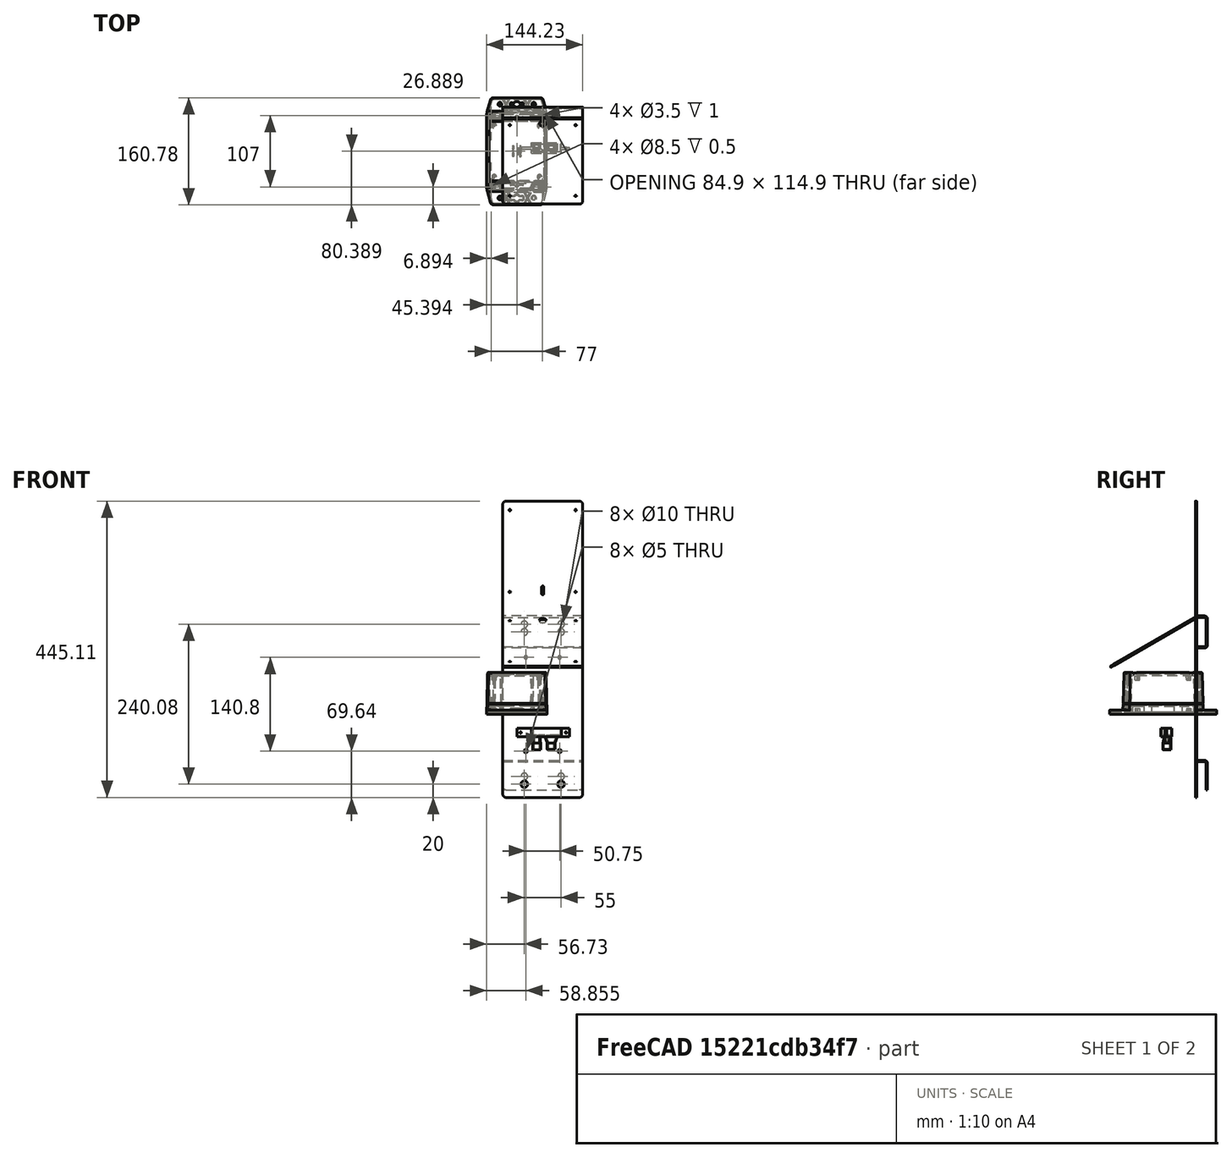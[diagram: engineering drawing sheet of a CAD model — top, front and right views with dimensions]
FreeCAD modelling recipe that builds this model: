
FCSTD DOCUMENT  (FreeCAD 0.19R24291 (Git))
Label: pzld_pm_vertical_wallmount
License: All rights reserved
LicenseURL: http://en.wikipedia.org/wiki/All_rights_reserved
objects: TechDraw::DrawViewDimension×19, Part::Feature×12, PartDesign::FeaturePython×10, Sketcher::SketchObject×7, TechDraw::DrawViewBalloon×4, TechDraw::DrawProjGroupItem×2, TechDraw::DrawProjGroup×2, PartDesign::Pad×1, App::Part×1, TechDraw::DrawSVGTemplate×1, TechDraw::DrawViewAnnotation×1, PartDesign::Fillet×1, PartDesign::Body×1, TechDraw::DrawPage×1
note: 34 computed .brp shape members not serialized (recipe doc carries the construction recipe); baked Part::Feature solids carry a one-line shape summary decoded from their .brp

FEATURE [Sketcher::SketchObject] Sketch
  FullyConstrained = true
  MapMode = 5
  Placement = pos=(0,0,0) rot=(1,0,0;1.5708rad)
  Support = -> [XZ_Plane]
  sketch-geometry (4):
    g0: LineSegment StartX=-60 StartY=-82.5 StartZ=0 EndX=60 EndY=-82.5 EndZ=0
    g1: LineSegment StartX=60 StartY=-82.5 StartZ=0 EndX=60 EndY=82.5 EndZ=0
    g2: LineSegment StartX=60 StartY=82.5 StartZ=0 EndX=-60 EndY=82.5 EndZ=0
    g3: LineSegment StartX=-60 StartY=82.5 StartZ=0 EndX=-60 EndY=-82.5 EndZ=0
  constraints (11):
    c: Coincident(g0,g1)
    c: Coincident(g1,g2)
    c: Coincident(g2,g3)
    c: Coincident(g3,g0)
    c: Horizontal(g0)
    c: Horizontal(g2)
    c: Vertical(g1)
    c: Vertical(g3)
    c: Symmetric(g1,g0,g-1)
    c: DistanceY(g3,g3) = 165
    c: DistanceX(g2,g2) = 120
FEATURE [PartDesign::Pad] Pad
  Direction = (1,1,1)
  Length = 2
  Length2 = 100
  Placement = pos=(0,0,0) rot=(1,0,0;1.5708rad)
  Profile = -> Sketch
  Type = 0
FEATURE [PartDesign::FeaturePython] Bend  label="Top to wall"  # WARN: FeaturePython — macro-defined, semantics opaque (R4)
  AutoMiter = true
  BaseFeature = -> Pad
  BendType = 0
  LengthList = [10]
  ReliefFactor = 0.7
  UseReliefFactor = false
  angle = 90
  baseObject = -> Pad [Edge10]
  bendAList = [90]
  extend1 = 0
  extend2 = 0
  gap1 = 0
  gap2 = 0
  invert = false
  kfactor = 0.5
  length = 10
  maxExtendDist = 5
  minGap = 0.1
  minReliefGap = 1
  miterangle1 = 0
  miterangle2 = 0
  offset = 0
  radius = 2
  reliefType = 0
  reliefd = 1
  reliefw = 0.8
  sketchflip = false
  sketchinvert = false
  unfold = false
FEATURE [PartDesign::FeaturePython] Bend001  label="Wall mount top"  # WARN: FeaturePython — macro-defined, semantics opaque (R4)
  AutoMiter = true
  BaseFeature = -> Bend
  BendType = 0
  LengthList = [40]
  ReliefFactor = 0.7
  UseReliefFactor = false
  angle = 90
  baseObject = -> Bend [Edge9]
  bendAList = [90]
  extend1 = 0
  extend2 = 0
  gap1 = 0
  gap2 = 0
  invert = true
  kfactor = 0.5
  length = 40
  maxExtendDist = 5
  minGap = 0.1
  minReliefGap = 1
  miterangle1 = 0
  miterangle2 = 0
  offset = 0
  radius = 2
  reliefType = 0
  reliefd = 1
  reliefw = 0.8
  sketchflip = false
  sketchinvert = false
  unfold = false
FEATURE [PartDesign::FeaturePython] Bend002  label="Top to solar"  # WARN: FeaturePython — macro-defined, semantics opaque (R4)
  AutoMiter = true
  BaseFeature = -> Bend001
  BendType = 0
  LengthList = [10]
  ReliefFactor = 0.7
  UseReliefFactor = false
  angle = 90
  baseObject = -> Bend001 [Edge9]
  bendAList = [90]
  extend1 = 0
  extend2 = 0
  gap1 = 0
  gap2 = 0
  invert = true
  kfactor = 0.5
  length = 10
  maxExtendDist = 5
  minGap = 0.1
  minReliefGap = 1
  miterangle1 = 0
  miterangle2 = 0
  offset = 0
  radius = 2
  reliefType = 0
  reliefd = 1
  reliefw = 0.8
  sketchflip = false
  sketchinvert = false
  unfold = false
FEATURE [PartDesign::FeaturePython] Bend003  label="Bottom to wall"  # WARN: FeaturePython — macro-defined, semantics opaque (R4)
  AutoMiter = true
  BaseFeature = -> Bend002
  BendType = 0
  LengthList = [10]
  ReliefFactor = 0.7
  UseReliefFactor = false
  angle = 90
  baseObject = -> Bend002 [Edge58]
  bendAList = [90]
  extend1 = 0
  extend2 = 0
  gap1 = 0
  gap2 = 0
  invert = true
  kfactor = 0.5
  length = 10
  maxExtendDist = 5
  minGap = 0.1
  minReliefGap = 1
  miterangle1 = 0
  miterangle2 = 0
  offset = 0
  radius = 2
  reliefType = 0
  reliefd = 1
  reliefw = 0.8
  sketchflip = false
  sketchinvert = false
  unfold = false
FEATURE [PartDesign::FeaturePython] Bend004  label="Solar"  # WARN: FeaturePython — macro-defined, semantics opaque (R4)
  AutoMiter = true
  BaseFeature = -> Bend003
  BendType = 0
  LengthList = [150]
  ReliefFactor = 0.7
  UseReliefFactor = false
  angle = 30
  baseObject = -> Bend003 [Edge75]
  bendAList = [30]
  extend1 = 0
  extend2 = 0
  gap1 = 0
  gap2 = 0
  invert = true
  kfactor = 0.5
  length = 150
  maxExtendDist = 5
  minGap = 0.1
  minReliefGap = 1
  miterangle1 = 0
  miterangle2 = 0
  offset = 0
  radius = 2
  reliefType = 0
  reliefd = 1
  reliefw = 0.8
  sketchflip = false
  sketchinvert = false
  unfold = false
FEATURE [PartDesign::FeaturePython] Bend005  label="Wall mount bottom"  # WARN: FeaturePython — macro-defined, semantics opaque (R4)
  AutoMiter = true
  BaseFeature = -> Bend004
  BendType = 0
  LengthList = [40]
  ReliefFactor = 0.7
  UseReliefFactor = false
  angle = 90
  baseObject = -> Bend004 [Edge91]
  bendAList = [90]
  extend1 = 0
  extend2 = 0
  gap1 = 0
  gap2 = 0
  invert = false
  kfactor = 0.5
  length = 40
  maxExtendDist = 5
  minGap = 0.1
  minReliefGap = 1
  miterangle1 = 0
  miterangle2 = 0
  offset = 0
  radius = 2
  reliefType = 0
  reliefd = 1
  reliefw = 0.8
  sketchflip = false
  sketchinvert = false
  unfold = false
FEATURE [Sketcher::SketchObject] Sketch001
  ExternalGeometry = -> [Bend005]
  FullyConstrained = true
  MapMode = 5
  Placement = pos=(0,-2,-4e-16) rot=(1,0,0;1.5708rad)
  Support = -> [Bend005]
  sketch-geometry (4):
    g0: Circle CenterX=-25.375 CenterY=70.4 CenterZ=0 NormalX=0 NormalY=0 NormalZ=1 AngleXU=0 Radius=2.5
    g1: Circle CenterX=25.375 CenterY=70.4 CenterZ=0 NormalX=0 NormalY=0 NormalZ=1 AngleXU=0 Radius=2.5
    g2: Circle CenterX=-25.375 CenterY=-70.4 CenterZ=0 NormalX=0 NormalY=0 NormalZ=1 AngleXU=0 Radius=2.5
    g3: Circle CenterX=25.375 CenterY=-70.4 CenterZ=0 NormalX=0 NormalY=0 NormalZ=1 AngleXU=0 Radius=2.5
  constraints (12):
    c: Equal(g3,g2)
    c: Equal(g2,g0)
    c: Equal(g0,g1)
    c: Vertical(g0,g2)
    c: Vertical(g1,g3)
    c: Horizontal(g0,g1)
    c: Horizontal(g3,g2)
    c: Symmetric(g0,g3,g-1)
    c: DistanceX(g0,g1) = 50.75
    c: DistanceY(g2,g0) = 140.8
    c: Diameter(g3) = 5
    c: DistanceY(g0,g-3) = -15.1679
FEATURE [PartDesign::FeaturePython] SketchOnSheet  label="Enclosure mount points"  # WARN: FeaturePython — macro-defined, semantics opaque (R4)
  BaseFeature = -> Bend005
  Sketch = -> Sketch001
  baseObject = -> Bend005 [Face20]
  kfactor = 0.5
FEATURE [Sketcher::SketchObject] Sketch002
  ExternalGeometry = -> [Bend001]
  FullyConstrained = true
  MapMode = 5
  Placement = pos=(0,14,5e-15) rot=(1,0,0;1.5708rad)
  Support = -> [SketchOnSheet]
  sketch-geometry (5):
    g0: GeomPoint X=-8.1e-15 Y=108.5 Z=0
    g1: Circle CenterX=-27.5 CenterY=108.5 CenterZ=0 NormalX=0 NormalY=0 NormalZ=1 AngleXU=0 Radius=5
    g2: Circle CenterX=27.5 CenterY=108.5 CenterZ=0 NormalX=0 NormalY=0 NormalZ=1 AngleXU=0 Radius=5
    g3: GeomPoint X=-22.5 Y=108.5 Z=0
    g4: GeomPoint X=22.5 Y=108.5 Z=0
  constraints (10):
    c: Symmetric(g-3,g-4,g0)
    c: Symmetric(g2,g1,g0)
    c: Horizontal(g1,g2)
    c: Equal(g2,g1)
    c: PointOnObject(g3,g1)
    c: PointOnObject(g4,g2)
    c: Horizontal(g4,g2)
    c: Horizontal(g1,g3)
    c: DistanceX(g3,g4) = 45
    c: Diameter(g1) = 10
FEATURE [PartDesign::FeaturePython] SketchOnSheet001  label="Wall mount points top"  # WARN: FeaturePython — macro-defined, semantics opaque (R4)
  BaseFeature = -> SketchOnSheet
  Sketch = -> Sketch002
  baseObject = -> SketchOnSheet [Face40]
  kfactor = 0.5
FEATURE [Sketcher::SketchObject] Sketch003
  ExternalGeometry = -> [SketchOnSheet001]
  FullyConstrained = true
  MapMode = 5
  Placement = pos=(0,14,1.6e-15) rot=(1,0,0;1.5708rad)
  Support = -> [SketchOnSheet001]
  sketch-geometry (5):
    g0: GeomPoint X=1.1e-15 Y=-108.5 Z=0
    g1: Circle CenterX=-27.5 CenterY=-108.5 CenterZ=0 NormalX=0 NormalY=0 NormalZ=1 AngleXU=0 Radius=5
    g2: Circle CenterX=27.5 CenterY=-108.5 CenterZ=0 NormalX=0 NormalY=0 NormalZ=1 AngleXU=0 Radius=5
    g3: GeomPoint X=-22.5 Y=-108.5 Z=0
    g4: GeomPoint X=22.5 Y=-108.5 Z=0
  constraints (10):
    c: Symmetric(g-3,g-4,g0)
    c: Symmetric(g2,g1,g0)
    c: Horizontal(g2,g1)
    c: PointOnObject(g3,g1)
    c: PointOnObject(g4,g2)
    c: Horizontal(g4,g2)
    c: Horizontal(g3,g1)
    c: DistanceX(g3,g4) = 45
    c: Diameter(g1) = 10
    c: Equal(g2,g1)
FEATURE [PartDesign::FeaturePython] SketchOnSheet002  label="Wall mount points bottom"  # WARN: FeaturePython — macro-defined, semantics opaque (R4)
  BaseFeature = -> SketchOnSheet001
  Sketch = -> Sketch003
  baseObject = -> SketchOnSheet001 [Face5]
  kfactor = 0.5
FEATURE [Sketcher::SketchObject] Sketch004
  ExternalGeometry = -> [SketchOnSheet002]
  FullyConstrained = true
  MapMode = 5
  Placement = pos=(0,-57.1421,98.9731) rot=(1,0,0;0.523599rad)
  Support = -> [SketchOnSheet002]
  sketch-geometry (8):
    g0: Circle CenterX=-49.4 CenterY=52.3821 CenterZ=0 NormalX=0 NormalY=0 NormalZ=1 AngleXU=0 Radius=1.5
    g1: Circle CenterX=49.4 CenterY=52.3821 CenterZ=0 NormalX=0 NormalY=0 NormalZ=1 AngleXU=0 Radius=1.5
    g2: Circle CenterX=49.4 CenterY=-70.4179 CenterZ=0 NormalX=0 NormalY=0 NormalZ=1 AngleXU=0 Radius=1.5
    g3: Circle CenterX=-49.4 CenterY=-70.4179 CenterZ=0 NormalX=0 NormalY=0 NormalZ=1 AngleXU=0 Radius=1.5
    g4: GeomPoint X=-1.5e-15 Y=-9.01795 Z=0
    g5: Circle CenterX=-6.1e-15 CenterY=55.0821 CenterZ=0 NormalX=0 NormalY=0 NormalZ=1 AngleXU=0 Radius=5
    g6: LineSegment StartX=-49.4 StartY=58.9821 StartZ=0 EndX=49.4 EndY=58.9821 EndZ=0
    g7: GeomPoint X=-6.1e-15 Y=58.9821 Z=0
  constraints (20):
    c: Equal(g3,g2)
    c: Equal(g2,g1)
    c: Equal(g1,g0)
    c: Diameter(g0) = 3
    c: DistanceX(g0,g1) = 98.8
    c: Vertical(g0,g3)
    c: Vertical(g2,g1)
    c: Horizontal(g2,g3)
    c: DistanceY(g2,g1) = 122.8
    c: Symmetric(g-3,g-4,g4)
    c: Symmetric(g1,g3,g4)
    c: Horizontal(g1,g0)
    c: Horizontal(g6)
    c: Vertical(g6,g0)
    c: Vertical(g6,g1)
    c: DistanceY(g1,g6) = 6.6
    c: Symmetric(g6,g6,g7)
    c: Vertical(g7,g5)
    c: DistanceY(g5,g7) = 3.9
    c: Diameter(g5) = 10
FEATURE [PartDesign::FeaturePython] SketchOnSheet003  label="Solar mount points"  # WARN: FeaturePython — macro-defined, semantics opaque (R4)
  BaseFeature = -> SketchOnSheet002
  Sketch = -> Sketch004
  baseObject = -> SketchOnSheet002 [Face59]
  kfactor = 0.5
FEATURE [Part::Feature] Part__Feature  label="1555FF LID"
  Placement = pos=(0,0,0) rot=(0,0,-1;1.5708rad)
  shape: bbox 90.8 x 160.8 x 370.5 mm, 927 faces (baked)
FEATURE [Part::Feature] Part__Feature001  label="1555FF42 BOX"
  Placement = pos=(-71.7099,-3.23523,0.5) rot=(0.707107,-0.707107,0;3.14159rad)
  shape: bbox 89.96 x 120 x 315.8 mm, 255 faces (baked)
FEATURE [Part::Feature] Part__Feature002  label="SC576 (screw M4-0.7X 20mm PN)"
  Placement = pos=(-77.3365,2.98878,-10) rot=(-0.862181,-0.358221,0.358221;1.71855rad)
  shape: bbox 7.373 x 7.373 x 22.24 mm, 29 faces (baked)
FEATURE [Part::Feature] Part__Feature003  label="SC576 (screw M4-0.7X 20mm PN)001"
  Placement = pos=(-0.336499,-104.011,-10) rot=(-0.170721,0.696726,-0.696726;2.80341rad)
  shape: bbox 7.033 x 7.033 x 22.24 mm, 29 faces (baked)
FEATURE [Part::Feature] Part__Feature004  label="SC576 (screw M4-0.7X 20mm PN)002"
  Placement = pos=(-0.336499,2.98878,-10) rot=(-0.98853,0.10679,-0.10679;1.58233rad)
  shape: bbox 7.203 x 7.203 x 22.24 mm, 29 faces (baked)
FEATURE [Part::Feature] Part__Feature005  label="SC576 (screw M4-0.7X 20mm PN)003"
  Placement = pos=(-77.3365,-104.011,-10) rot=(0.201011,0.692674,-0.692674;3.53833rad)
  shape: bbox 7.194 x 7.194 x 22.24 mm, 29 faces (baked)
FEATURE [Part::Feature] Part__Feature006  label="IN-M4 (insert M4-0.7X5.75mm SS)"
  Placement = pos=(-0.336499,2.98878,6.85) rot=(-1,0,0;1.5708rad)
  shape: bbox 6.35 x 6.35 x 6.35 mm, 16 faces (baked)
FEATURE [Part::Feature] Part__Feature007  label="IN-M4 (insert M4-0.7X5.75mm SS)001"
  Placement = pos=(-77.3365,2.98878,6.85) rot=(-1,0,0;1.5708rad)
  shape: bbox 6.35 x 6.35 x 6.35 mm, 16 faces (baked)
FEATURE [Part::Feature] Part__Feature008  label="IN-M4 (insert M4-0.7X5.75mm SS)002"
  Placement = pos=(-0.336499,-104.011,6.85) rot=(-1,0,0;1.5708rad)
  shape: bbox 6.35 x 6.35 x 6.35 mm, 16 faces (baked)
FEATURE [Part::Feature] Part__Feature009  label="IN-M4 (insert M4-0.7X5.75mm SS)003"
  Placement = pos=(-77.3365,-104.011,6.85) rot=(-1,0,0;1.5708rad)
  shape: bbox 6.35 x 6.35 x 6.35 mm, 16 faces (baked)
FEATURE [App::Part] _555FF42  label="1555FF42"
  Group = -> [Part__Feature,Part__Feature001,Part__Feature002,Part__Feature003,Part__Feature004,Part__Feature005,Part__Feature006,Part__Feature007,Part__Feature008,Part__Feature009]
  Origin = -> Origin001
  Placement = pos=(39,-17,50) rot=(1,0,0;1.5708rad)
FEATURE [Part::Feature] Unfold
  shape: bbox 120 x 2 x 445.1 mm, 26 faces (baked)
FEATURE [Sketcher::SketchObject] Unfold_Sketch
  FullyConstrained = false
  sketch-geometry (30):
    g0: ArcOfCircle CenterX=135.04 CenterY=-55 CenterZ=0 NormalX=0 NormalY=0 NormalZ=1 AngleXU=0 Radius=5 StartAngle=4.71239 EndAngle=6.28319
    g1: LineSegment StartX=140.04 StartY=-55 StartZ=0 EndX=140.04 EndY=55 EndZ=0
    g2: ArcOfCircle CenterX=135.04 CenterY=55 CenterZ=0 NormalX=0 NormalY=0 NormalZ=1 AngleXU=0 Radius=5 StartAngle=0 EndAngle=1.5708
    g3: ArcOfCircle CenterX=-300.066 CenterY=-55 CenterZ=0 NormalX=0 NormalY=0 NormalZ=1 AngleXU=-3.14159 Radius=5 StartAngle=0 EndAngle=1.5708
    g4: LineSegment StartX=-305.066 StartY=55 StartZ=0 EndX=-305.066 EndY=-55 EndZ=0
    g5: ArcOfCircle CenterX=-300.066 CenterY=55 CenterZ=0 NormalX=0 NormalY=0 NormalZ=1 AngleXU=-3.14159 Radius=5 StartAngle=4.71239 EndAngle=6.28319
    g6: Circle CenterX=120.04 CenterY=27.5 CenterZ=0 NormalX=0 NormalY=0 NormalZ=1 AngleXU=1.5708 Radius=5
    g7: Circle CenterX=120.04 CenterY=-27.5 CenterZ=0 NormalX=0 NormalY=0 NormalZ=1 AngleXU=1.5708 Radius=5
    g8: Circle CenterX=-120.04 CenterY=27.5 CenterZ=0 NormalX=0 NormalY=0 NormalZ=1 AngleXU=1.5708 Radius=5
    g9: Circle CenterX=-120.04 CenterY=-27.5 CenterZ=0 NormalX=0 NormalY=0 NormalZ=1 AngleXU=1.5708 Radius=5
    g10: LineSegment StartX=-175.966 StartY=-1.65 StartZ=0 EndX=-165.966 EndY=-1.65 EndZ=0
    g11: ArcOfCircle CenterX=-165.966 CenterY=0 CenterZ=0 NormalX=0 NormalY=0 NormalZ=1 AngleXU=1.5708 Radius=1.65 StartAngle=3.14159 EndAngle=6.28319
    g12: LineSegment StartX=-175.966 StartY=1.65 StartZ=0 EndX=-165.966 EndY=1.65 EndZ=0
    g13: ArcOfCircle CenterX=-175.966 CenterY=0 CenterZ=0 NormalX=0 NormalY=0 NormalZ=1 AngleXU=1.5708 Radius=1.65 StartAngle=0 EndAngle=3.14159
    g14: Circle CenterX=-70.4 CenterY=-25.375 CenterZ=0 NormalX=0 NormalY=0 NormalZ=1 AngleXU=1.5708 Radius=2.5
    g15: Circle CenterX=70.4 CenterY=-25.375 CenterZ=0 NormalX=0 NormalY=0 NormalZ=1 AngleXU=1.5708 Radius=2.5
    g16: Circle CenterX=-70.4 CenterY=25.375 CenterZ=0 NormalX=0 NormalY=0 NormalZ=1 AngleXU=1.5708 Radius=2.5
    g17: Circle CenterX=70.4 CenterY=25.375 CenterZ=0 NormalX=0 NormalY=0 NormalZ=1 AngleXU=1.5708 Radius=2.5
    g18: Circle CenterX=-168.666 CenterY=49.4 CenterZ=0 NormalX=0 NormalY=0 NormalZ=-1 AngleXU=1.5708 Radius=1.2
    g19: Circle CenterX=-291.466 CenterY=49.4 CenterZ=0 NormalX=0 NormalY=0 NormalZ=-1 AngleXU=1.5708 Radius=1.2
    g20: Circle CenterX=-168.666 CenterY=-49.4 CenterZ=0 NormalX=0 NormalY=0 NormalZ=-1 AngleXU=1.5708 Radius=1.2
    g21: Circle CenterX=-291.466 CenterY=-49.4 CenterZ=0 NormalX=0 NormalY=0 NormalZ=-1 AngleXU=1.5708 Radius=1.2
    g22: LineSegment StartX=-300.066 StartY=-60 StartZ=0 EndX=135.04 EndY=-60 EndZ=0
    g23: LineSegment StartX=135.04 StartY=60 StartZ=0 EndX=-300.066 EndY=60 EndZ=0
    g24: LineSegment StartX=98.1549 StartY=-60 StartZ=0 EndX=98.1549 EndY=60 EndZ=0
    g25: LineSegment StartX=84.385 StartY=-60 StartZ=0 EndX=84.385 EndY=60 EndZ=0
    g26: LineSegment StartX=-154.438 StartY=-60 StartZ=0 EndX=-154.438 EndY=60 EndZ=0
    g27: LineSegment StartX=-141.925 StartY=-60 StartZ=0 EndX=-141.925 EndY=60 EndZ=0
    g28: LineSegment StartX=-98.1549 StartY=-60 StartZ=0 EndX=-98.1549 EndY=60 EndZ=0
    g29: LineSegment StartX=-84.385 StartY=-60 StartZ=0 EndX=-84.385 EndY=60 EndZ=0
FEATURE [Part::Feature] Part__Feature010  label="Mount V2"
  Placement = pos=(-16.7,-53.7,-36.1) rot=(-1,0,0;1.5708rad)
  shape: bbox 79 x 16.3 x 32.5 mm, 81 faces (baked)
FEATURE [TechDraw::DrawSVGTemplate] Template
  EditableTexts = Designed_by_Name=<owner> B.V.; Drawing_number=1/1; FC-Date=2022-04-27; FC-SC=1:3; FC-SH=1/1; FC-Title=Multiflexmeter Mount; Subtitle=Pole & Wall mount w/ Solar; Weight=?
  Height = 210
  Orientation = 1
  Width = 297
FEATURE [TechDraw::DrawProjGroupItem] ProjItem  label="Left"
  CoarseView = false
  Direction = (-1,0,0)
  Focus = 100
  HardHidden = false
  IsoCount = 0
  IsoHidden = false
  IsoVisible = false
  LockPosition = true
  Perspective = false
  Rotation = 0
  RotationVector = (0,-1,0)
  ScaleType = 2
  SeamHidden = false
  SeamVisible = true
  SmoothHidden = false
  SmoothVisible = true
  Source = -> [SketchOnSheet003]
  Type = 1
  X = 0
  XDirection = (0,-1,0)
  Y = 0
FEATURE [TechDraw::DrawProjGroup] ProjGroup
  Anchor = -> ProjItem
  AutoDistribute = true
  LockPosition = false
  ProjectionType = 0
  Rotation = 0
  Scale = 0.333333
  ScaleType = 0
  Source = -> [SketchOnSheet003]
  Views = -> [ProjItem]
  X = 232.143
  Y = 120.146
  spacingX = 15
  spacingY = 15
FEATURE [TechDraw::DrawViewDimension] Dimension
  Arbitrary = false
  ArbitraryTolerances = false
  EqualTolerance = true
  FormatSpec = %.2f
  FormatSpecOverTolerance = %+.2f
  FormatSpecUnderTolerance = %+.2f
  Inverted = false
  LockPosition = false
  MeasureType = 1
  OverTolerance = 0
  References2D = -> [ProjItem]
  Rotation = 0
  Scale = 0.333333
  ScaleType = 0
  TheoreticalExact = false
  Type = 2
  UnderTolerance = 0
  X = -32.6559
  Y = -0.230905
FEATURE [TechDraw::DrawViewDimension] Dimension001
  Arbitrary = false
  ArbitraryTolerances = false
  EqualTolerance = true
  FormatSpec = %.2f
  FormatSpecOverTolerance = %+.2f
  FormatSpecUnderTolerance = %+.2f
  Inverted = false
  LockPosition = false
  MeasureType = 1
  OverTolerance = 0
  References2D = -> [ProjItem]
  Rotation = 0
  Scale = 0.333333
  ScaleType = 0
  TheoreticalExact = false
  Type = 2
  UnderTolerance = 0
  X = -32.9033
  Y = -35.0307
FEATURE [TechDraw::DrawViewDimension] Dimension002
  Arbitrary = false
  ArbitraryTolerances = false
  EqualTolerance = true
  FormatSpec = %.2f
  FormatSpecOverTolerance = %+.2f
  FormatSpecUnderTolerance = %+.2f
  Inverted = false
  LockPosition = false
  MeasureType = 1
  OverTolerance = 0
  References2D = -> [ProjItem]
  Rotation = 0
  Scale = 0.333333
  ScaleType = 0
  TheoreticalExact = false
  Type = 2
  UnderTolerance = 0
  X = -32.7745
  Y = 37.5951
FEATURE [TechDraw::DrawViewDimension] Dimension003
  Arbitrary = false
  ArbitraryTolerances = false
  EqualTolerance = true
  FormatSpec = %.2f
  FormatSpecOverTolerance = %+.2f
  FormatSpecUnderTolerance = %+.2f
  Inverted = false
  LockPosition = false
  MeasureType = 1
  OverTolerance = 0
  References2D = -> [ProjItem]
  Rotation = 0
  Scale = 0.333333
  ScaleType = 0
  TheoreticalExact = false
  Type = 0
  UnderTolerance = 0
  X = 11.2863
  Y = 42.5754
FEATURE [TechDraw::DrawViewAnnotation] Annotation
  Font = osifont
  LineSpace = 80
  LockPosition = false
  MaxWidth = -1
  Rotation = 0
  Scale = 0.333333
  ScaleType = 0
  Text = Inner dimension have priority over outer dimensions | Total length may deviate
  TextSize = 5
  TextStyle = 0
  X = 229.201
  Y = 190.726
FEATURE [TechDraw::DrawViewDimension] Dimension004
  Arbitrary = false
  ArbitraryTolerances = false
  EqualTolerance = false
  FormatSpec = %.2f
  FormatSpecOverTolerance = %+.2f
  FormatSpecUnderTolerance = %+.2f
  Inverted = false
  LockPosition = false
  MeasureType = 1
  OverTolerance = 10
  References2D = -> [ProjItem]
  Rotation = 0
  Scale = 0.333333
  ScaleType = 0
  TheoreticalExact = false
  Type = 1
  UnderTolerance = 0
  X = -47.3962
  Y = 55.1841
FEATURE [TechDraw::DrawViewDimension] Dimension005
  Arbitrary = false
  ArbitraryTolerances = false
  EqualTolerance = true
  FormatSpec = %.2f
  FormatSpecOverTolerance = %+.2f
  FormatSpecUnderTolerance = %+.2f
  Inverted = false
  LockPosition = false
  MeasureType = 1
  OverTolerance = 0
  References2D = -> [ProjItem]
  Rotation = 0
  Scale = 0.333333
  ScaleType = 0
  TheoreticalExact = false
  Type = 6
  UnderTolerance = 0
  X = -8.25137
  Y = 25.8566
FEATURE [TechDraw::DrawViewDimension] Dimension006
  Arbitrary = false
  ArbitraryTolerances = false
  EqualTolerance = true
  FormatSpec = %.2f
  FormatSpecOverTolerance = %+.2f
  FormatSpecUnderTolerance = %+.2f
  Inverted = false
  LockPosition = false
  MeasureType = 1
  OverTolerance = 0
  References2D = -> [ProjItem]
  Rotation = 0
  Scale = 0.333333
  ScaleType = 0
  TheoreticalExact = false
  Type = 1
  UnderTolerance = 0
  X = -14.5807
  Y = -43.6959
FEATURE [PartDesign::Fillet] Fillet
  Base = -> SketchOnSheet003 [Edge2,Edge8,Edge142,Edge124]
  BaseFeature = -> SketchOnSheet003
  Radius = 5
  SupportTransform = false
FEATURE [PartDesign::Body] Body  label="Wallmount"
  Group = -> [Sketch,Pad,Bend,Bend001,Bend002,Bend003,Bend004,Bend005,Sketch001,SketchOnSheet,Sketch002,SketchOnSheet001,Sketch003,SketchOnSheet002,Sketch004,SketchOnSheet003,Fillet]
  Origin = -> Origin
  Tip = -> Fillet
FEATURE [Sketcher::SketchObject] Unfold_Sketch001
  FullyConstrained = false
  sketch-geometry (27):
    g0: ArcOfCircle CenterX=136.296 CenterY=-55 CenterZ=0 NormalX=0 NormalY=0 NormalZ=1 AngleXU=0 Radius=5 StartAngle=4.71239 EndAngle=6.28319
    g1: LineSegment StartX=141.296 StartY=-55 StartZ=0 EndX=141.296 EndY=55 EndZ=0
    g2: ArcOfCircle CenterX=136.296 CenterY=55 CenterZ=0 NormalX=0 NormalY=0 NormalZ=1 AngleXU=0 Radius=5 StartAngle=0 EndAngle=1.5708
    g3: ArcOfCircle CenterX=-302.161 CenterY=-55 CenterZ=0 NormalX=0 NormalY=0 NormalZ=1 AngleXU=-3.14159 Radius=5 StartAngle=0 EndAngle=1.5708
    g4: LineSegment StartX=-307.161 StartY=55 StartZ=0 EndX=-307.161 EndY=-55 EndZ=0
    g5: ArcOfCircle CenterX=-302.161 CenterY=55 CenterZ=0 NormalX=0 NormalY=0 NormalZ=1 AngleXU=-3.14159 Radius=5 StartAngle=4.71239 EndAngle=6.28319
    g6: Circle CenterX=121.296 CenterY=27.5 CenterZ=0 NormalX=0 NormalY=0 NormalZ=1 AngleXU=1.5708 Radius=5
    g7: Circle CenterX=121.296 CenterY=-27.5 CenterZ=0 NormalX=0 NormalY=0 NormalZ=1 AngleXU=1.5708 Radius=5
    g8: Circle CenterX=-121.296 CenterY=27.5 CenterZ=0 NormalX=0 NormalY=0 NormalZ=1 AngleXU=1.5708 Radius=5
    g9: Circle CenterX=-121.296 CenterY=-27.5 CenterZ=0 NormalX=0 NormalY=0 NormalZ=1 AngleXU=1.5708 Radius=5
    g10: Circle CenterX=-168.061 CenterY=-6.1e-15 CenterZ=0 NormalX=0 NormalY=0 NormalZ=-1 AngleXU=1.5708 Radius=5
    g11: Circle CenterX=-70.4 CenterY=-25.375 CenterZ=0 NormalX=0 NormalY=0 NormalZ=1 AngleXU=1.5708 Radius=2.5
    g12: Circle CenterX=70.4 CenterY=-25.375 CenterZ=0 NormalX=0 NormalY=0 NormalZ=1 AngleXU=1.5708 Radius=2.5
    g13: Circle CenterX=-70.4 CenterY=25.375 CenterZ=0 NormalX=0 NormalY=0 NormalZ=1 AngleXU=1.5708 Radius=2.5
    g14: Circle CenterX=70.4 CenterY=25.375 CenterZ=0 NormalX=0 NormalY=0 NormalZ=1 AngleXU=1.5708 Radius=2.5
    g15: Circle CenterX=-170.761 CenterY=49.4 CenterZ=0 NormalX=0 NormalY=0 NormalZ=-1 AngleXU=1.5708 Radius=1.5
    g16: Circle CenterX=-293.561 CenterY=49.4 CenterZ=0 NormalX=0 NormalY=0 NormalZ=-1 AngleXU=1.5708 Radius=1.5
    g17: Circle CenterX=-170.761 CenterY=-49.4 CenterZ=0 NormalX=0 NormalY=0 NormalZ=-1 AngleXU=1.5708 Radius=1.5
    g18: Circle CenterX=-293.561 CenterY=-49.4 CenterZ=0 NormalX=0 NormalY=0 NormalZ=-1 AngleXU=1.5708 Radius=1.5
    g19: LineSegment StartX=-302.161 StartY=-60 StartZ=0 EndX=136.296 EndY=-60 EndZ=0
    g20: LineSegment StartX=136.296 StartY=60 StartZ=0 EndX=-302.161 EndY=60 EndZ=0
    g21: LineSegment StartX=99.0973 StartY=-60 StartZ=0 EndX=99.0973 EndY=60 EndZ=0
    g22: LineSegment StartX=84.6991 StartY=-60 StartZ=0 EndX=84.6991 EndY=60 EndZ=0
    g23: LineSegment StartX=-156.428 StartY=-60 StartZ=0 EndX=-156.428 EndY=60 EndZ=0
    g24: LineSegment StartX=-143.496 StartY=-60 StartZ=0 EndX=-143.496 EndY=60 EndZ=0
    g25: LineSegment StartX=-99.0973 StartY=-60 StartZ=0 EndX=-99.0973 EndY=60 EndZ=0
    g26: LineSegment StartX=-84.6991 StartY=-60 StartZ=0 EndX=-84.6991 EndY=60 EndZ=0
FEATURE [TechDraw::DrawProjGroupItem] ProjItem001  label="Flat"
  CoarseView = false
  Direction = (0,0,1)
  Focus = 100
  HardHidden = false
  IsoCount = 0
  IsoHidden = false
  IsoVisible = false
  LockPosition = true
  Perspective = false
  Rotation = 270
  RotationVector = (1,0,0)
  ScaleType = 2
  SeamHidden = false
  SeamVisible = true
  SmoothHidden = false
  SmoothVisible = true
  Source = -> [Unfold_Sketch001]
  Type = 0
  X = 0
  XDirection = (1,0,0)
  Y = 0
FEATURE [TechDraw::DrawProjGroup] ProjGroup001
  Anchor = -> ProjItem001
  AutoDistribute = true
  LockPosition = false
  ProjectionType = 0
  Rotation = 0
  Scale = 0.333333
  ScaleType = 0
  Source = -> [Unfold_Sketch001]
  Views = -> [ProjItem001]
  X = 61.7507
  Y = 102.543
  spacingX = 15
  spacingY = 15
FEATURE [TechDraw::DrawViewDimension] Dimension008
  Arbitrary = false
  ArbitraryTolerances = false
  EqualTolerance = true
  FormatSpec = %.2f
  FormatSpecOverTolerance = %+.2f
  FormatSpecUnderTolerance = %+.2f
  Inverted = false
  LockPosition = false
  MeasureType = 1
  OverTolerance = 0
  References2D = -> [ProjItem001]
  Rotation = 0
  Scale = 0.333333
  ScaleType = 0
  TheoreticalExact = false
  Type = 1
  UnderTolerance = 0
  X = -0.340106
  Y = 86.5346
FEATURE [TechDraw::DrawViewDimension] Dimension009
  Arbitrary = false
  ArbitraryTolerances = false
  EqualTolerance = true
  FormatSpec = %.2f
  FormatSpecOverTolerance = %+.2f
  FormatSpecUnderTolerance = %+.2f
  Inverted = false
  LockPosition = false
  MeasureType = 1
  OverTolerance = 0
  References2D = -> [ProjItem001]
  Rotation = 0
  Scale = 0.333333
  ScaleType = 0
  TheoreticalExact = false
  Type = 2
  UnderTolerance = 0
  X = -30.5944
  Y = 50.4582
FEATURE [TechDraw::DrawViewDimension] Dimension010
  Arbitrary = false
  ArbitraryTolerances = false
  EqualTolerance = true
  FormatSpec = %.2f
  FormatSpecOverTolerance = %+.2f
  FormatSpecUnderTolerance = %+.2f
  Inverted = false
  LockPosition = false
  MeasureType = 1
  OverTolerance = 0
  References2D = -> [ProjItem001]
  Rotation = 0
  Scale = 0.333333
  ScaleType = 0
  TheoreticalExact = false
  Type = 1
  UnderTolerance = 0
  X = -30.001
  Y = 22.5011
FEATURE [TechDraw::DrawViewDimension] Dimension011
  Arbitrary = false
  ArbitraryTolerances = false
  EqualTolerance = true
  FormatSpec = ⌀%.2f
  FormatSpecOverTolerance = %+.2f
  FormatSpecUnderTolerance = %+.2f
  Inverted = false
  LockPosition = false
  MeasureType = 1
  OverTolerance = 0
  References2D = -> [ProjItem001]
  Rotation = 0
  Scale = 0.333333
  ScaleType = 0
  TheoreticalExact = false
  Type = 5
  UnderTolerance = 0
  X = 30.9795
  Y = 33.3916
FEATURE [TechDraw::DrawViewDimension] Dimension012
  Arbitrary = false
  ArbitraryTolerances = false
  EqualTolerance = true
  FormatSpec = ⌀%.2f
  FormatSpecOverTolerance = %+.2f
  FormatSpecUnderTolerance = %+.2f
  Inverted = false
  LockPosition = false
  MeasureType = 1
  OverTolerance = 0
  References2D = -> [ProjItem001]
  Rotation = 0
  Scale = 0.333333
  ScaleType = 0
  TheoreticalExact = false
  Type = 5
  UnderTolerance = 0
  X = 30.9023
  Y = 18.1336
FEATURE [TechDraw::DrawViewDimension] Dimension013
  Arbitrary = false
  ArbitraryTolerances = false
  EqualTolerance = true
  FormatSpec = %.2f
  FormatSpecOverTolerance = %+.2f
  FormatSpecUnderTolerance = %+.2f
  Inverted = false
  LockPosition = false
  MeasureType = 1
  OverTolerance = 0
  References2D = -> [ProjItem001]
  Rotation = 0
  Scale = 0.333333
  ScaleType = 0
  TheoreticalExact = false
  Type = 1
  UnderTolerance = 0
  X = -30.7252
  Y = 4.1445
FEATURE [TechDraw::DrawViewDimension] Dimension014
  Arbitrary = false
  ArbitraryTolerances = false
  EqualTolerance = true
  FormatSpec = ⌀%.2f
  FormatSpecOverTolerance = %+.2f
  FormatSpecUnderTolerance = %+.2f
  Inverted = false
  LockPosition = false
  MeasureType = 1
  OverTolerance = 0
  References2D = -> [ProjItem001]
  Rotation = 0
  Scale = 0.333333
  ScaleType = 0
  TheoreticalExact = false
  Type = 5
  UnderTolerance = 0
  X = 31.1483
  Y = 1.17541
FEATURE [TechDraw::DrawViewDimension] Dimension015
  Arbitrary = false
  ArbitraryTolerances = false
  EqualTolerance = true
  FormatSpec = R%.2f
  FormatSpecOverTolerance = %+.2f
  FormatSpecUnderTolerance = %+.2f
  Inverted = false
  LockPosition = false
  MeasureType = 1
  OverTolerance = 0
  References2D = -> [ProjItem001]
  Rotation = 0
  Scale = 0.333333
  ScaleType = 0
  TheoreticalExact = false
  Type = 4
  UnderTolerance = 0
  X = 26.7356
  Y = 85.6
FEATURE [TechDraw::DrawViewDimension] Dimension016
  Arbitrary = false
  ArbitraryTolerances = false
  EqualTolerance = true
  FormatSpec = ⌀%.2f
  FormatSpecOverTolerance = %+.2f
  FormatSpecUnderTolerance = %+.2f
  Inverted = false
  LockPosition = false
  MeasureType = 1
  OverTolerance = 0
  References2D = -> [ProjItem001]
  Rotation = 0
  Scale = 0.333333
  ScaleType = 0
  TheoreticalExact = false
  Type = 5
  UnderTolerance = 0
  X = 29.4324
  Y = 75.3998
FEATURE [TechDraw::DrawViewDimension] Dimension017
  Arbitrary = false
  ArbitraryTolerances = false
  EqualTolerance = true
  FormatSpec = %.2f
  FormatSpecOverTolerance = %+.2f
  FormatSpecUnderTolerance = %+.2f
  Inverted = false
  LockPosition = false
  MeasureType = 1
  OverTolerance = 0
  References2D = -> [ProjItem001]
  Rotation = 0
  Scale = 0.333333
  ScaleType = 0
  TheoreticalExact = false
  Type = 2
  UnderTolerance = 0
  X = -30.1799
  Y = -25.9515
FEATURE [TechDraw::DrawViewDimension] Dimension018
  Arbitrary = false
  ArbitraryTolerances = false
  EqualTolerance = true
  FormatSpec = %.2f
  FormatSpecOverTolerance = %+.2f
  FormatSpecUnderTolerance = %+.2f
  Inverted = false
  LockPosition = false
  MeasureType = 1
  OverTolerance = 0
  References2D = -> [ProjItem001]
  Rotation = 0
  Scale = 0.333333
  ScaleType = 0
  TheoreticalExact = false
  Type = 1
  UnderTolerance = 0
  X = -35.6854
  Y = -58.3438
FEATURE [TechDraw::DrawViewDimension] Dimension019
  Arbitrary = false
  ArbitraryTolerances = false
  EqualTolerance = true
  FormatSpec = ⌀%.2f
  FormatSpecOverTolerance = %+.2f
  FormatSpecUnderTolerance = %+.2f
  Inverted = false
  LockPosition = false
  MeasureType = 1
  OverTolerance = 0
  References2D = -> [ProjItem001]
  Rotation = 0
  Scale = 0.333333
  ScaleType = 0
  TheoreticalExact = false
  Type = 5
  UnderTolerance = 0
  X = 31.2314
  Y = -63.1248
FEATURE [TechDraw::DrawViewBalloon] Balloon
  BubbleShape = 0
  EndType = 0
  EndTypeScale = 1
  KinkLength = 5
  LockPosition = false
  OriginX = 45.66
  OriginY = -231.047
  Rotation = 0
  Scale = 0.333333
  ScaleType = 0
  ShapeScale = 1
  SourceView = -> ProjItem001
  Text = #1
  TextWrapLen = -1
  X = 90.7037
  Y = -259.442
FEATURE [TechDraw::DrawViewBalloon] Balloon001
  BubbleShape = 0
  EndType = 0
  EndTypeScale = 1
  KinkLength = 5
  LockPosition = false
  OriginX = 65.4628
  OriginY = 156.31
  Rotation = 0
  Scale = 0.333333
  ScaleType = 0
  ShapeScale = 1
  SourceView = -> ProjItem001
  Text = #2
  TextWrapLen = -1
  X = 156.797
  Y = 174.979
FEATURE [TechDraw::DrawViewBalloon] Balloon002
  BubbleShape = 0
  EndType = 0
  EndTypeScale = 1
  KinkLength = 5
  LockPosition = false
  OriginX = -66.793
  OriginY = -112.165
  Rotation = 0
  Scale = 0.333333
  ScaleType = 0
  ShapeScale = 1
  SourceView = -> ProjItem
  Text = #1
  TextWrapLen = -1
  X = 22.2589
  Y = -92.4054
FEATURE [TechDraw::DrawViewBalloon] Balloon003
  BubbleShape = 0
  EndType = 0
  EndTypeScale = 1
  KinkLength = 5
  LockPosition = false
  OriginX = 39.3322
  OriginY = 62.0024
  Rotation = 0
  Scale = 0.333333
  ScaleType = 0
  ShapeScale = 1
  SourceView = -> ProjItem
  Text = #2
  TextWrapLen = -1
  X = 79.9823
  Y = -0.444541
FEATURE [TechDraw::DrawPage] Page
  KeepUpdated = true
  NextBalloonIndex = 6
  ProjectionType = 0
  Scale = 0.333333
  Template = -> Template
  Views = -> [ProjGroup,Dimension,Dimension001,Dimension002,Dimension003,Annotation,Dimension004,Dimension005,Dimension006,ProjGroup001,Dimension008,Dimension009,Dimension010,Dimension011,Dimension012,Dimension013,Dimension014,Dimension015,Dimension016,Dimension017,Dimension018,Dimension019,Balloon,Balloon001,Balloon002,Balloon003]
  expr: Scale = 1 / 3
